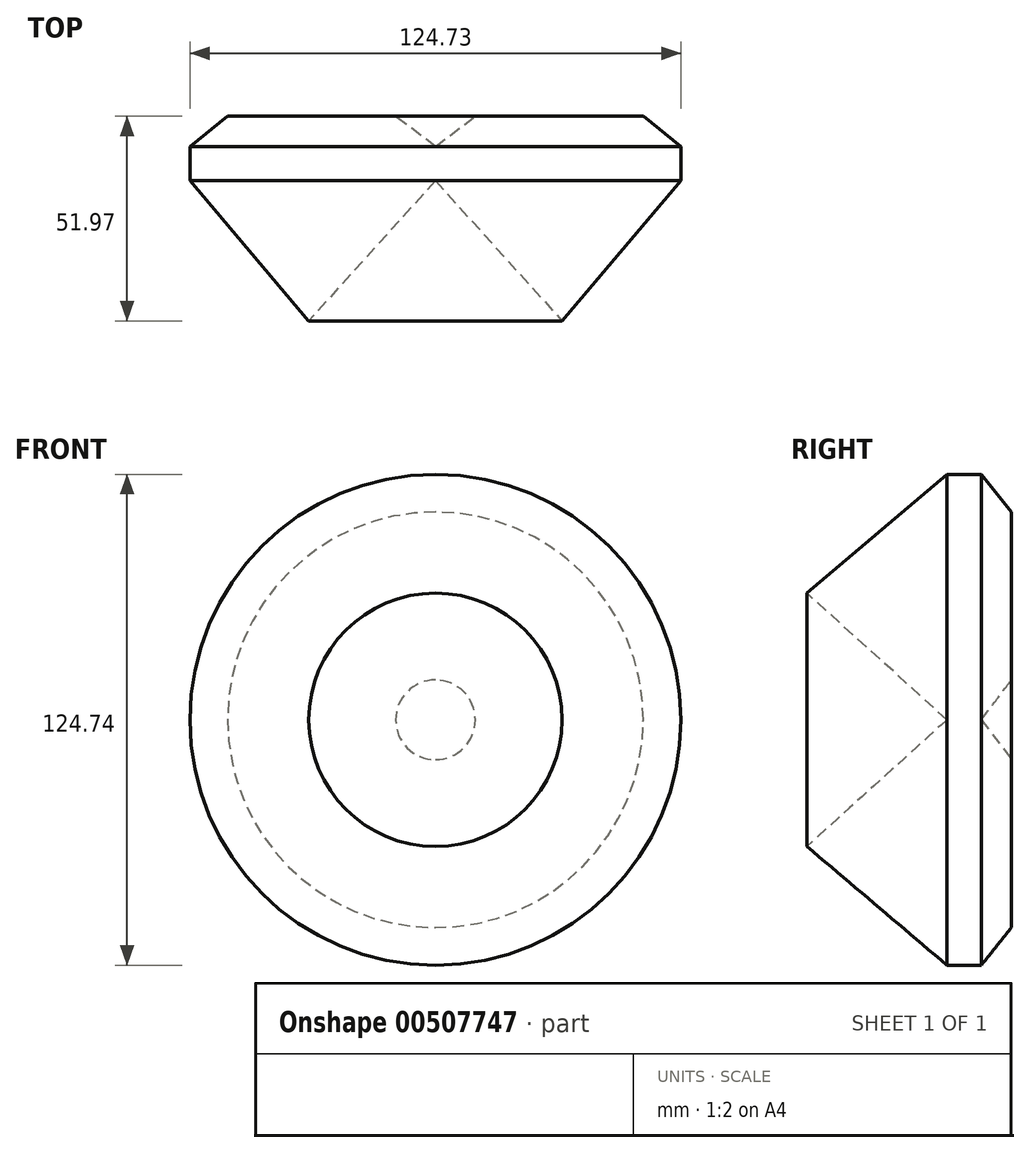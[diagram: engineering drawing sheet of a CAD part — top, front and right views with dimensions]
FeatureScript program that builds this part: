
annotation { "Feature Type Name" : "Feature", "Feature Type Description" : "" }
export const myFeature = defineFeature(function(context is Context, id is Id, definition is map)
    precondition{}
    {
        {
            var Q0;
            Q0=qCreatedBy(makeId("Top.planeOp"),FACE);
            var sketch = newSketch(context, id + "F0", { "sketchPlane" : qUnion([Q0])});
            skLineSegment(sketch, "E0", {"start": v(-32.18, 0) * mm, "end": v(-32.18, 8.74) * mm});
            skLineSegment(sketch, "E1", {"start": v(-32.18, 8.74) * mm, "end": v(-22.06, 16.4) * mm});
            skLineSegment(sketch, "E2", {"start": v(-22.06, 16.4) * mm, "end": v(20.61, 16.4) * mm});
            skLineSegment(sketch, "E3", {"start": v(20.61, 16.4) * mm, "end": v(30.19, 8.74) * mm});
            skLineSegment(sketch, "E4", {"start": v(30.19, 8.74) * mm, "end": v(30.19, 0) * mm});
            skLineSegment(sketch, "E5", {"start": v(-32.18, 0) * mm, "end": v(0, -35.57) * mm});
            skLineSegment(sketch, "E6", {"start": v(30.19, 0) * mm, "end": v(0, -35.57) * mm});
            skSolve(sketch);
        }
        {
            var Q0;
            Q0=makeQuery(id+"F0.imprint","IMPRINT",FACE,{"disambiguationData":[TD([[makeQuery(id+"F0.imprint","IMPRINT",EDGE,{"derivedFrom":sQuery(id+"F0.wireOp",EDGE,"E0")}),-1.0]])]});
            var Q1;
            Q1=sQuery(id+"F0.wireOp",EDGE,"E0");
            revolve(context, id + "F1", {"entities" : qUnion([Q0]), "axis" : qUnion([Q1]), "revolveType" : RevolveType.FULL});
        }
    });
